# Revit family: ME_Оборудование [водосчетчик универсальный (новый) без сгонов VLF-15U-L]1 - VALTEC
name_source: partatom
category: Оборудование
units: mm (PartAtom-declared; Revit-internal decimal feet)

## family parameters
Всегда вертикально = Да
Классификация = Нет
На основе рабочей плоскости = Нет
Общий = Нет
При загрузке вырезать с полостями = Нет
Размер круглого соединителя = Использовать диаметр
Тип детали = Вставляется
Точка расчета площади = Нет

## types (2) — shared parameters
ADSK_URL документации изделия = https://valtec.ru
ADSK_URL страницы изделия = https://valtec.ru
ADSK_Материал = Сталь, нержавеющая - VALTEC
ADSK_Потеря давления жидкости = 250.0 Па
ADSK_Расход жидкости = 0.0 л/с
D = 15 мм
URL = https://valtec.ru
d1 = 15 мм
d2 = 10 мм
d3 = 10 мм
l = 80 мм
Изготовитель = VALTEC
Материал доб.1 = Пластик серый - VALTEC
Материал доб.2 = Пластик белый - VALTEC
Материал доб.3 = Пластик прозрачный - VALTEC
Материал доб.4 = Красной - VALTEC
Показать направление потока = Нет
Таблица = ME_Оборудование [водосчетчик универсальный (новый) без сгонов VLF-15U-L] - VALTEC

## per-type parameters (varying)
| type | n |
| 80 мм | 0 мм |
| 110 мм | 1 мм |

note: column(s) folded — value = type name in every type: L
